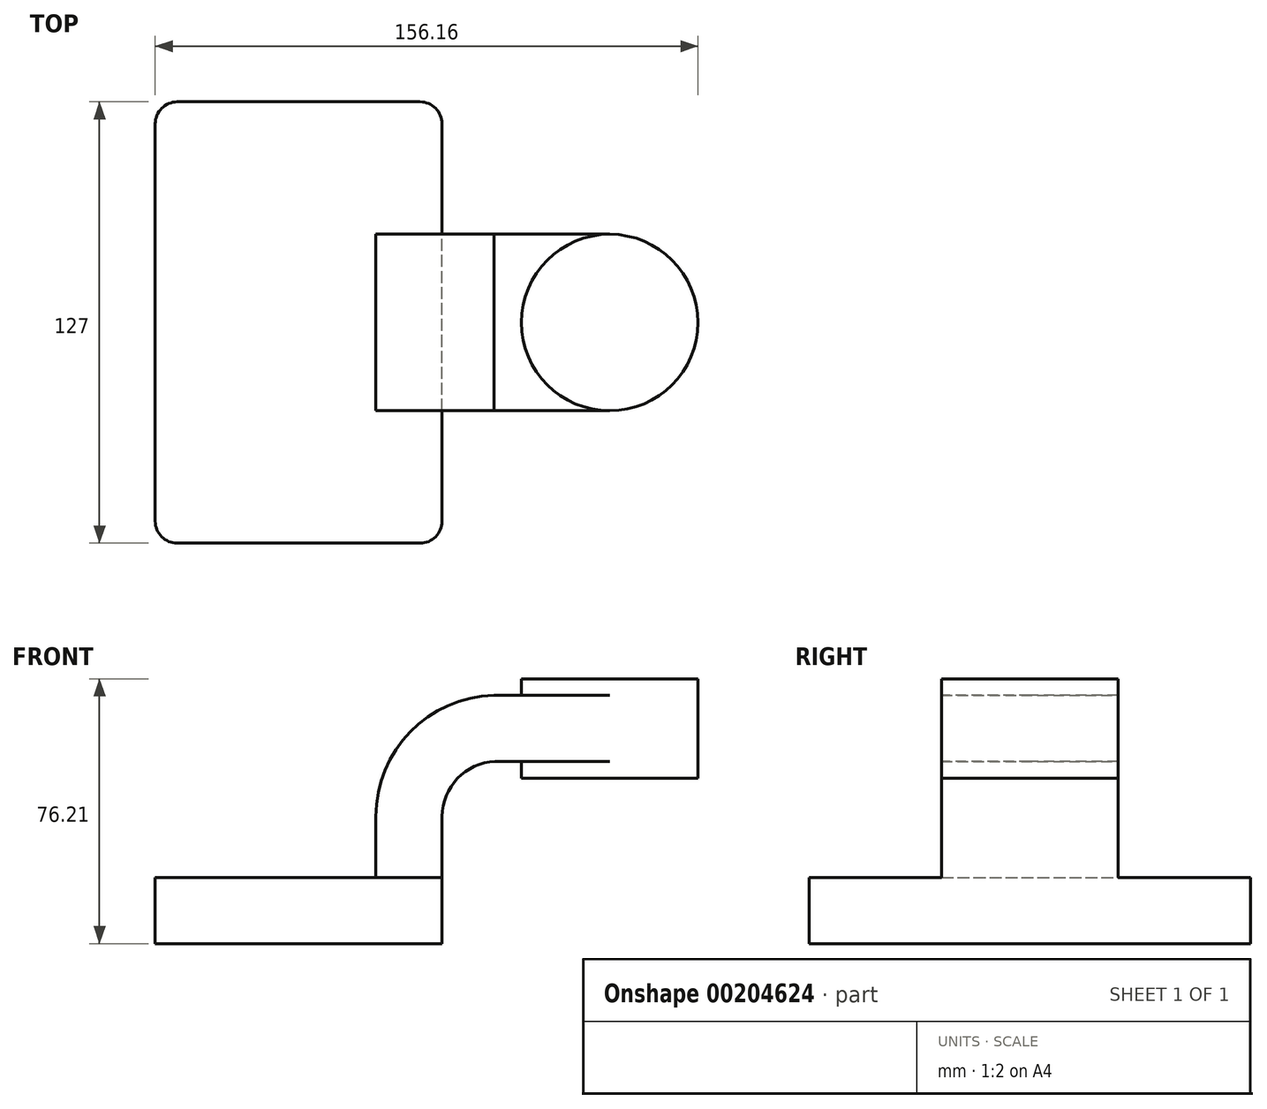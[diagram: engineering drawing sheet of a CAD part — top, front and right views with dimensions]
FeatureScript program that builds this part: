
annotation { "Feature Type Name" : "Feature", "Feature Type Description" : "" }
export const myFeature = defineFeature(function(context is Context, id is Id, definition is map)
    precondition{}
    {
        {
            var Q0;
            Q0=qCreatedBy(makeId("Front.planeOp"),FACE);
            var sketch = newSketch(context, id + "F0", { "sketchPlane" : qUnion([Q0])});
            skLineSegment(sketch, "E0.bottom", {"start": v(-41.28, 9.52) * mm, "end": v(41.27, 9.53) * mm});
            skLineSegment(sketch, "E0.top", {"start": v(-41.28, -9.52) * mm, "end": v(41.28, -9.52) * mm});
            skLineSegment(sketch, "E0.left", {"start": v(-41.28, 9.52) * mm, "end": v(-41.28, -9.53) * mm});
            skLineSegment(sketch, "E0.right", {"start": v(41.27, 9.53) * mm, "end": v(41.28, -9.52) * mm});
            skPoint(sketch, "E0.middle", {"position": v(0, 0) * mm});
            skLineSegment(sketch, "E1.bottom", {"start": v(64.09, 66.68) * mm, "end": v(114.89, 66.68) * mm});
            skLineSegment(sketch, "E1.top", {"start": v(64.09, 38.1) * mm, "end": v(114.89, 38.1) * mm});
            skLineSegment(sketch, "E1.left", {"start": v(64.09, 66.68) * mm, "end": v(64.09, 38.1) * mm});
            skLineSegment(sketch, "E1.right", {"start": v(114.89, 66.68) * mm, "end": v(114.89, 38.1) * mm});
            skPoint(sketch, "E1.middle", {"position": v(89.49, 52.39) * mm});
            skLineSegment(sketch, "E2", {"start": v(41.27, 9.53) * mm, "end": v(41.27, 27.01) * mm});
            skArc(sketch, "E3", {"start": v(41.27, 27.01) * mm, "mid": v(45.7, 38) * mm, "end": v(56.5, 42.88) * mm});
            skLineSegment(sketch, "E4", {"start": v(56.5, 42.88) * mm, "end": v(89.49, 42.88) * mm});
            skPoint(sketch, "E4.endSnap0", {"position": v(89.49, 38.1) * mm});
            skLineSegment(sketch, "E5.0", {"start": v(56.2, 61.93) * mm, "end": v(89.49, 61.93) * mm});
            skArc(sketch, "E5.1", {"start": v(22.22, 27.01) * mm, "mid": v(32.12, 51.37) * mm, "end": v(56.2, 61.93) * mm});
            skLineSegment(sketch, "E5.2", {"start": v(22.22, 9.53) * mm, "end": v(22.22, 27.01) * mm});
            skLineSegment(sketch, "E6", {"start": v(89.49, 38.1) * mm, "end": v(89.49, 66.68) * mm});
            skFitSpline(sketch, "E7", {"points": [v(-41.28, 9.52) * mm, v(56.2, 61.93) * mm], "startDerivative": vector(42.48, 102.28) * mm, "endDerivative": vector(121.24, -15) * mm});
            skSolve(sketch);
        }
        {
            var Q0;
            Q0=makeQuery(id+"F0.imprint","IMPRINT",FACE,{"disambiguationData":[TD([[makeQuery(id+"F0.imprint","IMPRINT",EDGE,{"derivedFrom":sQuery(id+"F0.wireOp",EDGE,"E0.top")}),1.0]])]});
            extrude(context, id + "F1", {"entities" : qUnion([Q0]), "endBound" : BoundingType.SYMMETRIC, "depth" : 127 * mm});
        }
        {
            var Q0;
            {var subQ1=sQuery(id+"F0.wireOp",EDGE,"E2");Q0=makeQuery(id+"F0.imprint","IMPRINT",FACE,{"disambiguationData":[TD([[makeQuery(id+"F0.imprint","IMPRINT",EDGE,{"derivedFrom":subQ1}),1.0]])]});}
            var Q1;
            {var subQ0=sQuery(id+"F0.wireOp",EDGE,"E5.0");var subQ1=sQuery(id+"F0.wireOp",EDGE,"E1.left");var subQ2=makeQuery(id+"F0.imprint","INTERSECT",VERTEX,{"derivedFrom":[subQ1,subQ0]});Q1=makeQuery(id+"F0.imprint","IMPRINT",FACE,{"disambiguationData":[TD([[makeQuery(id+"F0.imprint","IMPRINT",EDGE,{"disambiguationData":[TD([[subQ2,-1.0]])],"derivedFrom":subQ1}),1.0]])]});}
            extrude(context, id + "F2", {"entities" : qUnion([Q0, Q1]), "operationType" : NewBodyOperationType.ADD, "endBound" : BoundingType.SYMMETRIC, "depth" : 50.8 * mm});
        }
        {
            var Q0;
            Q0=makeQuery(id+"F0.imprint","IMPRINT",FACE,{"disambiguationData":[TD([[makeQuery(id+"F0.imprint","IMPRINT",EDGE,{"derivedFrom":sQuery(id+"F0.wireOp",EDGE,"E5.1")}),1.0]])]});
            extrude(context, id + "F3", {"entities" : qUnion([Q0]), "operationType" : NewBodyOperationType.ADD, "endBound" : BoundingType.SYMMETRIC, "depth" : 15.88 * mm});
        }
        {
            var Q0;
            {var subQ0=sQuery(id+"F0.wireOp",EDGE,"E1.right");Q0=makeQuery(id+"F0.imprint","IMPRINT",FACE,{"disambiguationData":[TD([[makeQuery(id+"F0.imprint","IMPRINT",EDGE,{"derivedFrom":subQ0}),-1.0]])]});}
            var Q1;
            Q1=sQuery(id+"F0.wireOp",EDGE,"E6");
            revolve(context, id + "F4", {"operationType" : NewBodyOperationType.ADD, "entities" : qUnion([Q0]), "axis" : qUnion([Q1]), "revolveType" : RevolveType.FULL});
        }
        {
            var Q0;
            Q0=makeQuery(id+"F1.opExtrude","CAP_EDGE",EDGE,{"disambiguationData":[OSD([sQuery(id+"F0.wireOp",EDGE,"E0.left")])],"isStart":false});
            var Q1;
            Q1=makeQuery(id+"F1.opExtrude","CAP_EDGE",EDGE,{"disambiguationData":[OSD([sQuery(id+"F0.wireOp",EDGE,"E0.right")])],"isStart":false});
            var Q2;
            Q2=makeQuery(id+"F1.opExtrude","CAP_EDGE",EDGE,{"disambiguationData":[OSD([sQuery(id+"F0.wireOp",EDGE,"E0.right")])],"isStart":true});
            var Q3;
            Q3=makeQuery(id+"F1.opExtrude","CAP_EDGE",EDGE,{"disambiguationData":[OSD([sQuery(id+"F0.wireOp",EDGE,"E0.left")])],"isStart":true});
            fillet(context, id + "F5", {"entities" : qUnion([Q0, Q1, Q2, Q3]), "radius" : 6.35 * mm, "tangentPropagation" : true, "allowEdgeOverflow" : false});
        }
    });
